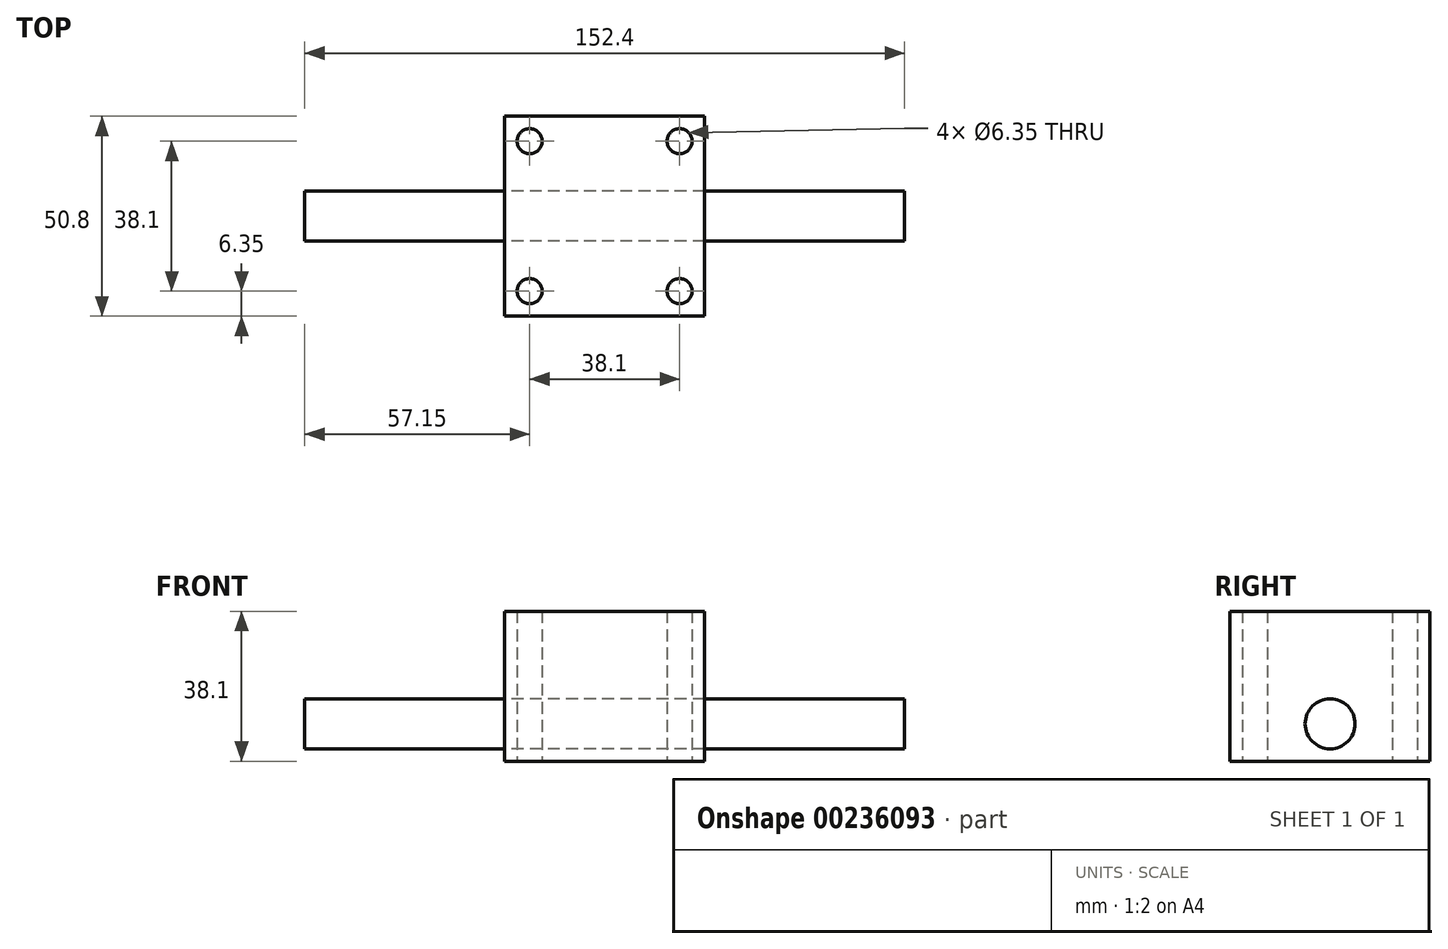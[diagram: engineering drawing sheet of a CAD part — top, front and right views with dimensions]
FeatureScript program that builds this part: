
annotation { "Feature Type Name" : "Feature", "Feature Type Description" : "" }
export const myFeature = defineFeature(function(context is Context, id is Id, definition is map)
    precondition{}
    {
        {
            var Q0;
            Q0=qCreatedBy(makeId("Top.planeOp"),FACE);
            var sketch = newSketch(context, id + "F0", { "sketchPlane" : qUnion([Q0])});
            skLineSegment(sketch, "E0.bottom", {"start": v(25.4, -25.4) * mm, "end": v(-25.4, -25.4) * mm});
            skLineSegment(sketch, "E0.top", {"start": v(25.4, 25.4) * mm, "end": v(-25.4, 25.4) * mm});
            skLineSegment(sketch, "E0.left", {"start": v(25.4, -25.4) * mm, "end": v(25.4, 25.4) * mm});
            skLineSegment(sketch, "E0.right", {"start": v(-25.4, -25.4) * mm, "end": v(-25.4, 25.4) * mm});
            skPoint(sketch, "E0.middle", {"position": v(0, 0) * mm});
            skCircle(sketch, "E1", {"center": v(-19.05, 19.05) * mm, "radius": 3.18 * mm});
            skCircle(sketch, "E2.MirrorC", {"center": v(19.05, 19.05) * mm, "radius": 3.18 * mm});
            skCircle(sketch, "E3.MirrorC", {"center": v(-19.05, -19.05) * mm, "radius": 3.18 * mm});
            skCircle(sketch, "E4.MirrorC", {"center": v(19.05, -19.05) * mm, "radius": 3.18 * mm});
            skSolve(sketch);
        }
        {
            var Q0;
            Q0 = qSketchRegion(id + "F0", true);
            extrude(context, id + "F1", {"entities" : qUnion([Q0]), "endBound" : BoundingType.SYMMETRIC, "depth" : 38.1 * mm});
        }
        {
            var Q0;
            Q0=qCreatedBy(makeId("Right.planeOp"),FACE);
            var sketch = newSketch(context, id + "F2", { "sketchPlane" : qUnion([Q0])});
            skCircle(sketch, "E5", {"center": v(0, -9.53) * mm, "radius": 6.35 * mm});
            skSolve(sketch);
        }
        {
            var Q0;
            Q0 = qSketchRegion(id + "F2", true);
            extrude(context, id + "F3", {"entities" : qUnion([Q0]), "endBound" : BoundingType.SYMMETRIC, "depth" : 152.4 * mm});
        }
    });
